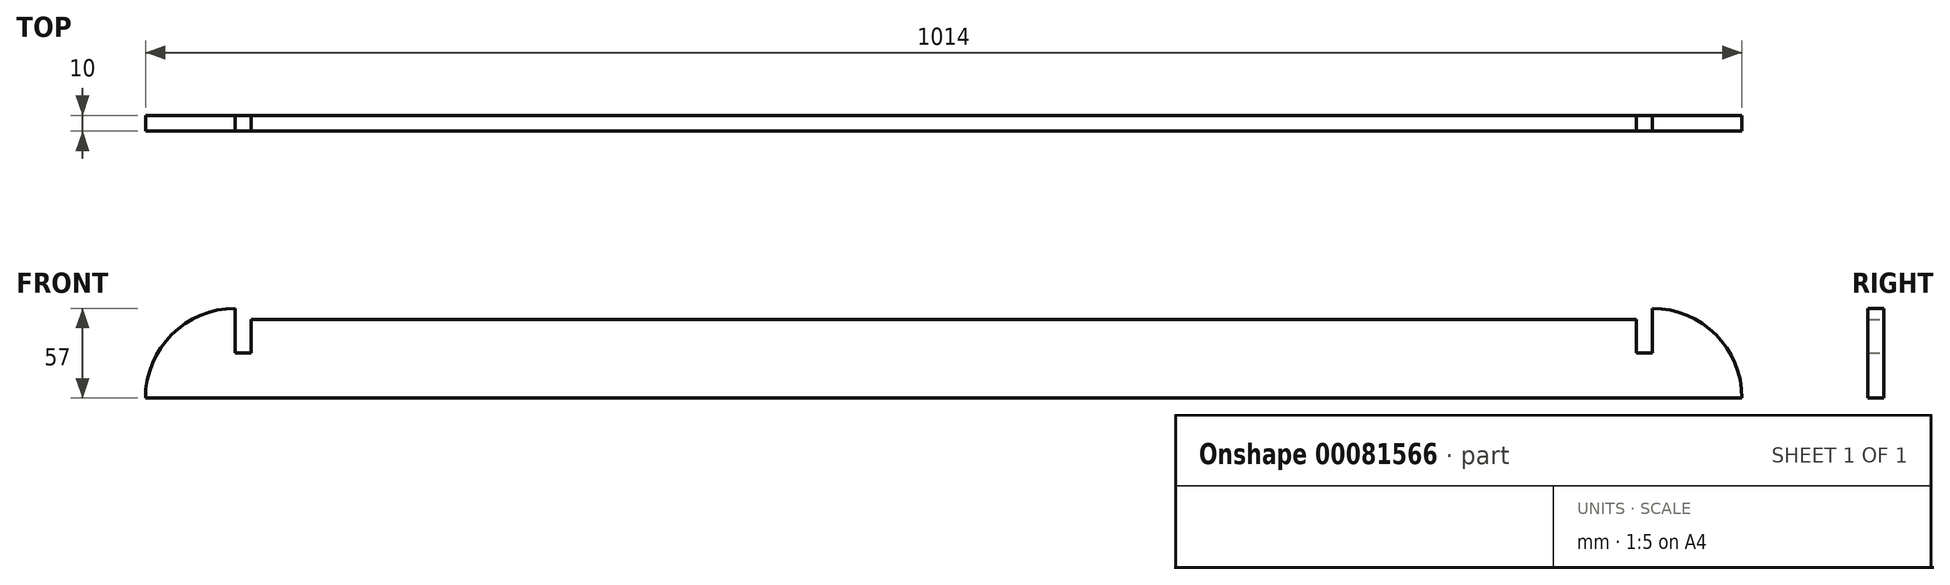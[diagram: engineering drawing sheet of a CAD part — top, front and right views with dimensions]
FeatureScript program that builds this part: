
annotation { "Feature Type Name" : "Feature", "Feature Type Description" : "" }
export const myFeature = defineFeature(function(context is Context, id is Id, definition is map)
    precondition{}
    {
        {
            var Q0;
            Q0=qCreatedBy(makeId("Front.planeOp"),FACE);
            var sketch = newSketch(context, id + "F0", { "sketchPlane" : qUnion([Q0])});
            skLineSegment(sketch, "E0", {"start": v(507, 0) * mm, "end": v(-507, 0) * mm});
            skArc(sketch, "E1", {"start": v(-450, 57) * mm, "mid": v(-490.3, 40.3) * mm, "end": v(-507, 0) * mm});
            skArc(sketch, "E2", {"start": v(507, 0) * mm, "mid": v(490.3, 40.3) * mm, "end": v(450, 57) * mm});
            skLineSegment(sketch, "E3", {"start": v(-450, 57) * mm, "end": v(-450, 28.5) * mm});
            skLineSegment(sketch, "E4", {"start": v(-450, 28.5) * mm, "end": v(-440, 28.5) * mm});
            skLineSegment(sketch, "E5", {"start": v(-440, 28.5) * mm, "end": v(-440, 50) * mm});
            skLineSegment(sketch, "E6", {"start": v(450, 57) * mm, "end": v(450, 28.5) * mm});
            skLineSegment(sketch, "E7", {"start": v(450, 28.5) * mm, "end": v(440, 28.5) * mm});
            skLineSegment(sketch, "E8", {"start": v(440, 28.5) * mm, "end": v(440, 50) * mm});
            skLineSegment(sketch, "E9", {"start": v(440, 50) * mm, "end": v(-440, 50) * mm});
            skLineSegment(sketch, "E10", {"start": v(-450, 57) * mm, "end": v(450, 57) * mm, "construction": true});
            skSolve(sketch);
        }
        {
            var Q0;
            Q0=qSketchRegion(id+"F0",true);
            extrude(context, id + "F1", {"entities" : qUnion([Q0]), "depth" : 10 * mm});
        }
    });
